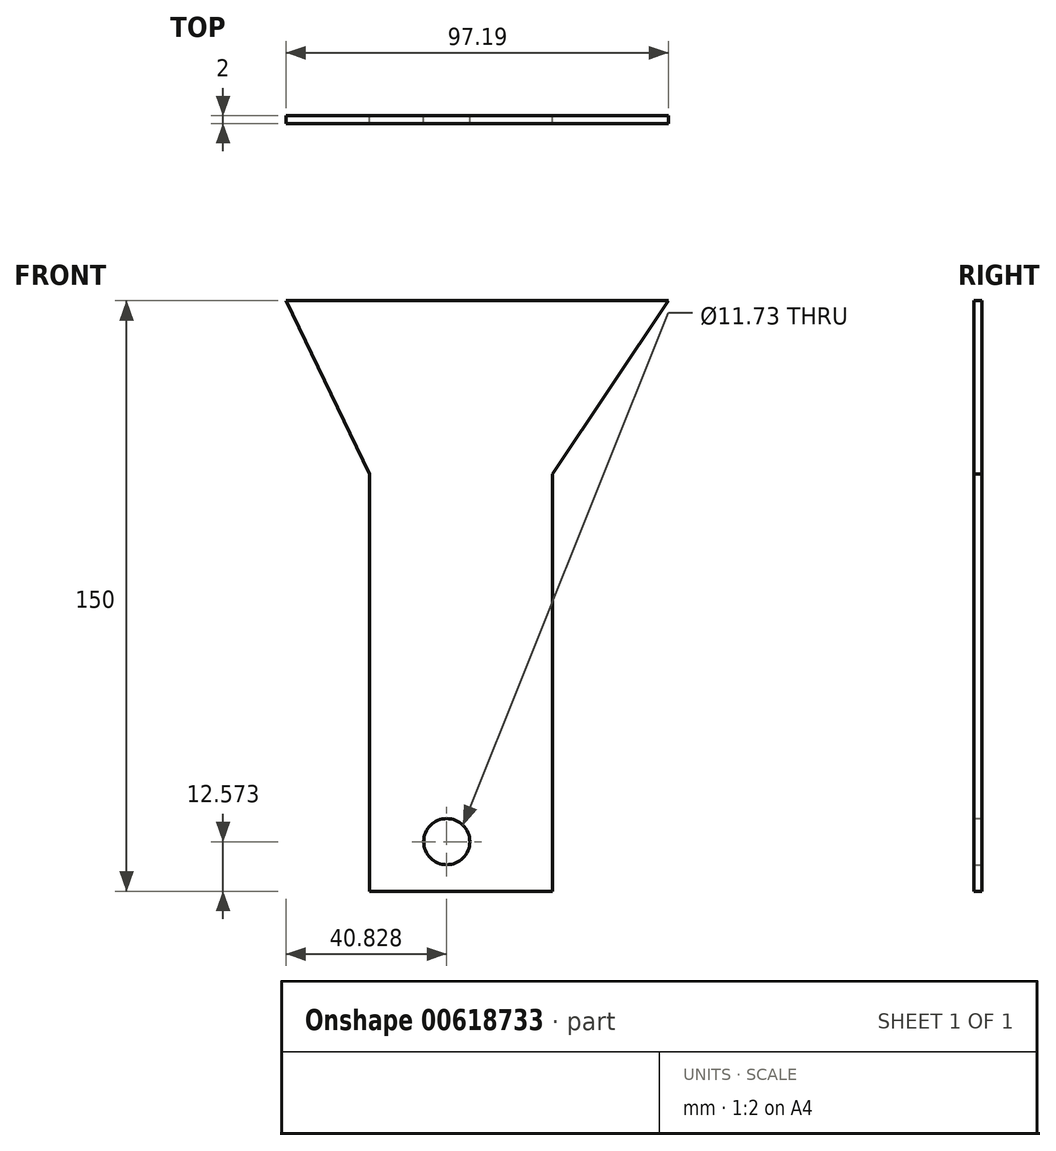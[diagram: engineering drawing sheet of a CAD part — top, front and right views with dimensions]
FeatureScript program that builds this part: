
annotation { "Feature Type Name" : "Feature", "Feature Type Description" : "" }
export const myFeature = defineFeature(function(context is Context, id is Id, definition is map)
    precondition{}
    {
        {
            var Q0;
            Q0=qCreatedBy(makeId("Front.planeOp"),FACE);
            var sketch = newSketch(context, id + "F0", { "sketchPlane" : qUnion([Q0])});
            skLineSegment(sketch, "E0.bottom", {"start": v(-49.5, 75) * mm, "end": v(49.5, 75) * mm});
            skLineSegment(sketch, "E0.top", {"start": v(-49.5, -75) * mm, "end": v(49.5, -75) * mm});
            skLineSegment(sketch, "E0.left", {"start": v(-49.5, 75) * mm, "end": v(-49.5, -75) * mm});
            skLineSegment(sketch, "E0.right", {"start": v(49.5, 75) * mm, "end": v(49.5, -75) * mm});
            skPoint(sketch, "E0.middle", {"position": v(0, 0) * mm});
            skSolve(sketch);
        }
        {
            var Q0;
            Q0 = qSketchRegion(id + "F0", true);
            extrude(context, id + "F1", {"entities" : qUnion([Q0]), "depth" : 1 * mm, "offsetDistance" : 25 * mm});
        }
        {
            var Q0;
            Q0=makeQuery(id+"F1.opExtrude","CAP_FACE",FACE,{"disambiguationData":[OSD([sQuery(id+"F0.wireOp",EDGE,"E0.bottom"),sQuery(id+"F0.wireOp",EDGE,"E0.top"),sQuery(id+"F0.wireOp",EDGE,"E0.left"),sQuery(id+"F0.wireOp",EDGE,"E0.right")])],"isStart":true});
            var sketch = newSketch(context, id + "F2", { "sketchPlane" : qUnion([Q0])});
            skCircle(sketch, "E1", {"center": v(6.86, -62.43) * mm, "radius": 5.86 * mm});
            skSolve(sketch);
        }
        {
            var Q0;
            Q0=makeQuery(id+"F1.opExtrude","CAP_FACE",FACE,{"disambiguationData":[OSD([sQuery(id+"F0.wireOp",EDGE,"E0.bottom"),sQuery(id+"F0.wireOp",EDGE,"E0.top"),sQuery(id+"F0.wireOp",EDGE,"E0.left"),sQuery(id+"F0.wireOp",EDGE,"E0.right")])],"isStart":false});
            var Q1;
            Q1 = qSketchRegion(id + "F2", true);
            extrude(context, id + "F3", {"entities" : qUnion([Q0, Q1]), "operationType" : NewBodyOperationType.ADD, "depth" : 1 * mm, "offsetDistance" : 25 * mm});
        }
        {
            var Q0;
            Q0 = qSketchRegion(id + "F2", true);
            extrude(context, id + "F4", {"entities" : qUnion([Q0]), "operationType" : NewBodyOperationType.REMOVE, "oppositeDirection" : true, "depth" : 25 * mm, "offsetDistance" : 25 * mm});
        }
        {
            var Q0;
            Q0=makeQuery(id+"F1.opExtrude","CAP_FACE",FACE,{"disambiguationData":[OSD([sQuery(id+"F0.wireOp",EDGE,"E0.bottom"),sQuery(id+"F0.wireOp",EDGE,"E0.top"),sQuery(id+"F0.wireOp",EDGE,"E0.left"),sQuery(id+"F0.wireOp",EDGE,"E0.right")])],"isStart":true});
            var sketch = newSketch(context, id + "F5", { "sketchPlane" : qUnion([Q0])});
            skLineSegment(sketch, "E2", {"start": v(-19.95, -75) * mm, "end": v(-19.95, 31) * mm});
            skLineSegment(sketch, "E3", {"start": v(-19.95, 31) * mm, "end": v(-49.5, 75) * mm});
            skLineSegment(sketch, "E4", {"start": v(26.5, -75) * mm, "end": v(26.5, 31) * mm});
            skLineSegment(sketch, "E5", {"start": v(26.5, 31) * mm, "end": v(49.5, 78.75) * mm});
            skLineSegment(sketch, "E6", {"start": v(-46.81, 71) * mm, "end": v(45.77, 71) * mm});
            skLineSegment(sketch, "E7", {"start": v(-23.7, 36.58) * mm, "end": v(31.3, 36.58) * mm});
            skLineSegment(sketch, "E8", {"start": v(31.3, 36.58) * mm, "end": v(29.19, 36.58) * mm});
            skSolve(sketch);
        }
        {
            var Q0;
            {var subQ4=sQuery(id+"F5.wireOp",EDGE,"E2");Q0=makeQuery(id+"F5.imprint","IMPRINT",FACE,{"disambiguationData":[TD([[makeQuery(id+"F5.imprint","IMPRINT",EDGE,{"derivedFrom":subQ4}),1.0]])]});}
            var Q1;
            {var subQ5=sQuery(id+"F5.wireOp",EDGE,"E4");Q1=makeQuery(id+"F5.imprint","IMPRINT",FACE,{"disambiguationData":[TD([[makeQuery(id+"F5.imprint","IMPRINT",EDGE,{"derivedFrom":subQ5}),-1.0]])]});}
            extrude(context, id + "F6", {"entities" : qUnion([Q0, Q1]), "operationType" : NewBodyOperationType.REMOVE, "oppositeDirection" : true, "depth" : 25 * mm, "offsetDistance" : 25 * mm});
        }
    });
